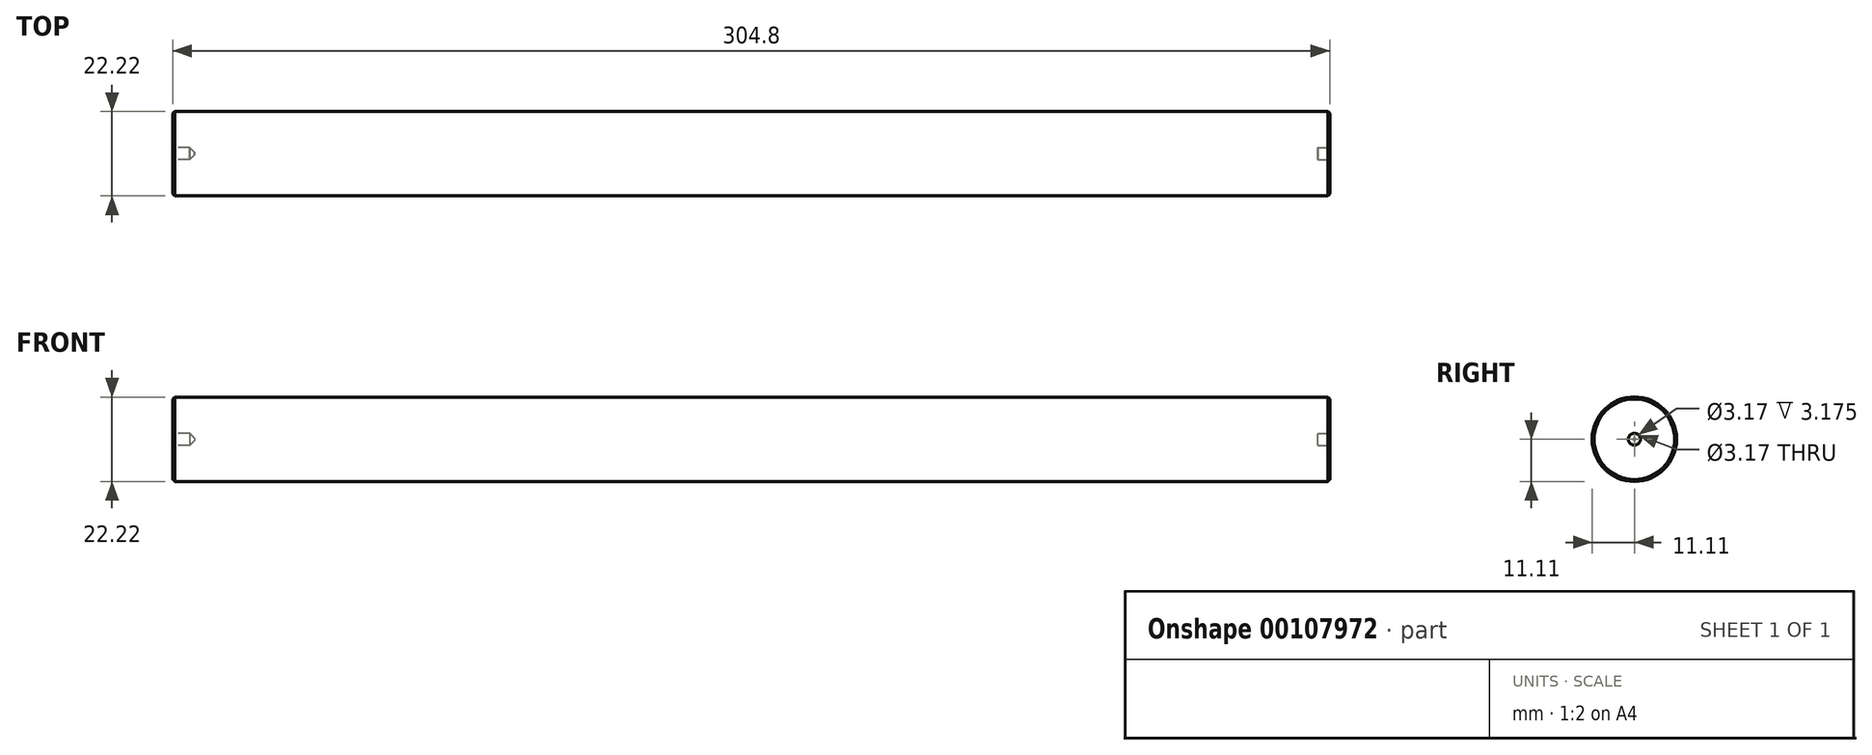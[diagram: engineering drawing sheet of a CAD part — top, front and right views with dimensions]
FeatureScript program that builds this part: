
annotation { "Feature Type Name" : "Feature", "Feature Type Description" : "" }
export const myFeature = defineFeature(function(context is Context, id is Id, definition is map)
    precondition{}
    {
        {
            var Q0;
            Q0=qCreatedBy(makeId("Right.planeOp"),FACE);
            var sketch = newSketch(context, id + "F0", { "sketchPlane" : qUnion([Q0])});
            skCircle(sketch, "E0", {"center": v(0, 0) * mm, "radius": 11.11 * mm});
            skSolve(sketch);
        }
        {
            var Q0;
            Q0=makeQuery(id+"F0.imprint","IMPRINT",FACE,{"disambiguationData":[TD([[makeQuery(id+"F0.imprint","IMPRINT",EDGE,{"derivedFrom":sQuery(id+"F0.wireOp",EDGE,"E0")}),1.0]])]});
            extrude(context, id + "F1", {"entities" : qUnion([Q0]), "depth" : 304.8 * mm});
        }
        {
            var Q0;
            Q0=makeQuery(id+"F1.opExtrude","CAP_FACE",FACE,{"disambiguationData":[OSD([sQuery(id+"F0.wireOp",EDGE,"E0")])],"isStart":false});
            var sketch = newSketch(context, id + "F2", { "sketchPlane" : qUnion([Q0])});
            skCircle(sketch, "E1", {"center": v(0, 0) * mm, "radius": 1.59 * mm});
            skSolve(sketch);
        }
        {
            var Q0;
            Q0=makeQuery(id+"F2.imprint","IMPRINT",FACE,{"disambiguationData":[TD([[makeQuery(id+"F2.imprint","IMPRINT",EDGE,{"derivedFrom":sQuery(id+"F2.wireOp",EDGE,"E1")}),1.0]])]});
            extrude(context, id + "F3", {"entities" : qUnion([Q0]), "operationType" : NewBodyOperationType.REMOVE, "oppositeDirection" : true, "depth" : 3.17 * mm});
        }
        {
            var Q0;
            Q0=makeQuery(id+"F1.opExtrude","CAP_FACE",FACE,{"disambiguationData":[OSD([sQuery(id+"F0.wireOp",EDGE,"E0")])],"isStart":true});
            var sketch = newSketch(context, id + "F4", { "sketchPlane" : qUnion([Q0])});
            skCircle(sketch, "E2", {"center": v(0, 0) * mm, "radius": 1.59 * mm});
            skSolve(sketch);
        }
        {
            var Q0;
            Q0=makeQuery(id+"F4.imprint","IMPRINT",FACE,{"disambiguationData":[TD([[makeQuery(id+"F4.imprint","IMPRINT",EDGE,{"derivedFrom":sQuery(id+"F4.wireOp",EDGE,"E2")}),1.0]])]});
            extrude(context, id + "F5", {"entities" : qUnion([Q0]), "operationType" : NewBodyOperationType.REMOVE, "oppositeDirection" : true, "depth" : 5.7 * mm});
        }
        {
            var Q0;
            Q0=makeQuery(id+"F1.opExtrude","CAP_EDGE",EDGE,{"disambiguationData":[OSD([sQuery(id+"F0.wireOp",EDGE,"E0")])],"isStart":true});
            var Q1;
            Q1=makeQuery(id+"F1.opExtrude","CAP_EDGE",EDGE,{"disambiguationData":[OSD([sQuery(id+"F0.wireOp",EDGE,"E0")])],"isStart":false});
            chamfer(context, id + "F6", {"entities" : qUnion([Q0, Q1]), "width" : 0.5 * mm, "tangentPropagation" : true});
        }
        {
            var Q0;
            Q0=makeQuery(id+"F3.boolean.opBoolean","COPY",EDGE,{"derivedFrom":makeQuery(id+"F3.opExtrude","CAP_EDGE",EDGE,{"disambiguationData":[OSD([sQuery(id+"F2.wireOp",EDGE,"E1")])],"isStart":true})});
            var Q1;
            Q1=makeQuery(id+"F5.boolean.opBoolean","COPY",EDGE,{"derivedFrom":makeQuery(id+"F5.opExtrude","CAP_EDGE",EDGE,{"disambiguationData":[OSD([sQuery(id+"F4.wireOp",EDGE,"E2")])],"isStart":false})});
            chamfer(context, id + "F7", {"entities" : qUnion([Q0, Q1]), "width" : 1.27 * mm, "tangentPropagation" : true});
        }
    });
